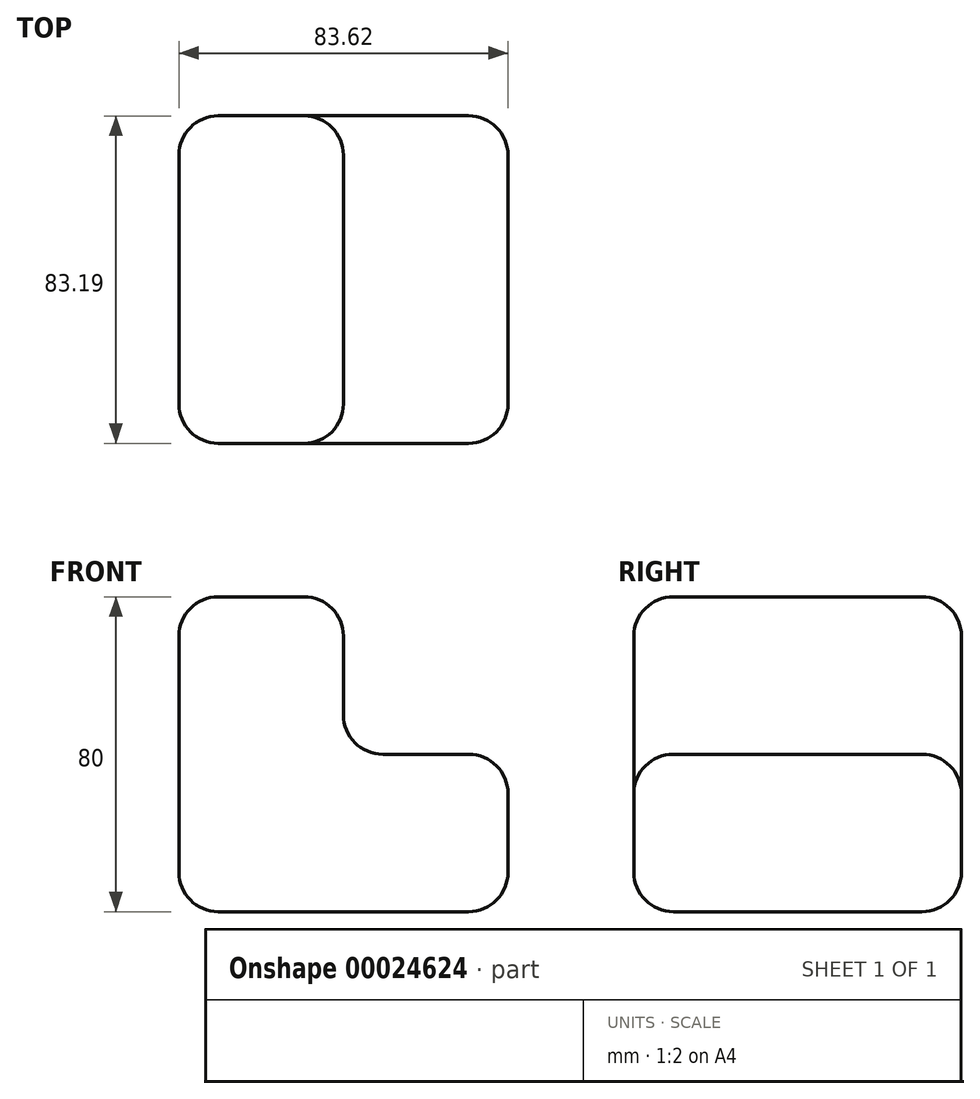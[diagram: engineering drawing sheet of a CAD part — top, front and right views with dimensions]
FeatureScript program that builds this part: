
annotation { "Feature Type Name" : "Feature", "Feature Type Description" : "" }
export const myFeature = defineFeature(function(context is Context, id is Id, definition is map)
    precondition{}
    {
        {
            var Q0;
            Q0=qCreatedBy(makeId("Top.planeOp"),FACE);
            var sketch = newSketch(context, id + "F0", { "sketchPlane" : qUnion([Q0])});
            skLineSegment(sketch, "E0.bottom", {"start": v(-59.13, -45.93) * mm, "end": v(24.5, -45.93) * mm});
            skLineSegment(sketch, "E0.top", {"start": v(-59.13, 37.26) * mm, "end": v(24.5, 37.26) * mm});
            skLineSegment(sketch, "E0.left", {"start": v(-59.13, -45.93) * mm, "end": v(-59.13, 37.26) * mm});
            skLineSegment(sketch, "E0.right", {"start": v(24.5, -45.93) * mm, "end": v(24.5, 37.26) * mm});
            skSolve(sketch);
        }
        {
            var Q0;
            Q0=makeQuery(id+"F0.imprint","IMPRINT",FACE,{"disambiguationData":[TD([[makeQuery(id+"F0.imprint","IMPRINT",EDGE,{"derivedFrom":sQuery(id+"F0.wireOp",EDGE,"E0.bottom")}),1.0]])]});
            extrude(context, id + "F1", {"entities" : qUnion([Q0]), "depth" : 40 * mm});
        }
        {
            var Q0;
            Q0=makeQuery(id+"F1.opExtrude","CAP_FACE",FACE,{"disambiguationData":[OSD([sQuery(id+"F0.wireOp",EDGE,"E0.bottom"),sQuery(id+"F0.wireOp",EDGE,"E0.top"),sQuery(id+"F0.wireOp",EDGE,"E0.left"),sQuery(id+"F0.wireOp",EDGE,"E0.right")])],"isStart":false});
            var sketch = newSketch(context, id + "F2", { "sketchPlane" : qUnion([Q0])});
            skLineSegment(sketch, "E1", {"start": v(-17.32, 37.26) * mm, "end": v(-17.32, -45.93) * mm});
            skSolve(sketch);
        }
        {
            var Q0;
            {var subQ1=sQuery(id+"F2.wireOp",EDGE,"E1");Q0=makeQuery(id+"F2.imprint","IMPRINT",FACE,{"disambiguationData":[TD([[makeQuery(id+"F2.imprint","IMPRINT",EDGE,{"derivedFrom":subQ1}),-1.0]])]});}
            extrude(context, id + "F3", {"entities" : qUnion([Q0]), "operationType" : NewBodyOperationType.ADD, "depth" : 40 * mm});
        }
        {
            var Q0;
            Q0=makeQuery(id+"F3.opExtrude","SWEPT_FACE",FACE,{"disambiguationData":[OSD([sQuery(id+"F2.wireOp",EDGE,"E1")])]});
            var Q1;
            Q1=makeQuery(id+"F3.opExtrude","SWEPT_EDGE",EDGE,{"disambiguationData":[OSD([sQuery(id+"F0.wireOp",EDGE,"E0.top"),sQuery(id+"F2.wireOp",EDGE,"E1")])]});
            var Q2;
            Q2=makeQuery(id+"F3.opExtrude","CAP_FACE",FACE,{"disambiguationData":[OSD([sQuery(id+"F0.wireOp",EDGE,"E0.bottom"),sQuery(id+"F0.wireOp",EDGE,"E0.top"),sQuery(id+"F0.wireOp",EDGE,"E0.left"),sQuery(id+"F2.wireOp",EDGE,"E1")])],"isStart":false});
            var Q3;
            Q3=makeQuery(id+"F3.opExtrude","SWEPT_EDGE",EDGE,{"disambiguationData":[OSD([sQuery(id+"F0.wireOp",EDGE,"E0.bottom"),sQuery(id+"F2.wireOp",EDGE,"E1")])]});
            var Q4;
            Q4=makeQuery(id+"F3.opExtrude","CAP_EDGE",EDGE,{"disambiguationData":[OSD([sQuery(id+"F2.wireOp",EDGE,"E1")])],"isStart":false});
            var Q5;
            {var subQ0=sQuery(id+"F0.wireOp",EDGE,"E0.bottom");Q5=makeQuery(id+"F3.boolean.opBoolean","MERGE",FACE,{"derivedFrom":[makeQuery(id+"F1.opExtrude","SWEPT_FACE",FACE,{"disambiguationData":[OSD([subQ0])]}),makeQuery(id+"F3.opExtrude","SWEPT_FACE",FACE,{"disambiguationData":[OSD([subQ0])]})]});}
            var Q6;
            {var subQ0=sQuery(id+"F0.wireOp",EDGE,"E0.bottom");var subQ1=sQuery(id+"F0.wireOp",EDGE,"E0.left");Q6=makeQuery(id+"F3.boolean.opBoolean","MERGE",EDGE,{"derivedFrom":[makeQuery(id+"F1.opExtrude","SWEPT_EDGE",EDGE,{"disambiguationData":[OSD([subQ0,subQ1])]}),makeQuery(id+"F3.opExtrude","SWEPT_EDGE",EDGE,{"disambiguationData":[OSD([subQ0,subQ1])]})]});}
            var Q7;
            Q7=makeQuery(id+"F3.opExtrude","CAP_EDGE",EDGE,{"disambiguationData":[OSD([sQuery(id+"F0.wireOp",EDGE,"E0.left")])],"isStart":false});
            var Q8;
            {var subQ0=sQuery(id+"F0.wireOp",EDGE,"E0.top");Q8=makeQuery(id+"F3.boolean.opBoolean","MERGE",FACE,{"derivedFrom":[makeQuery(id+"F1.opExtrude","SWEPT_FACE",FACE,{"disambiguationData":[OSD([subQ0])]}),makeQuery(id+"F3.opExtrude","SWEPT_FACE",FACE,{"disambiguationData":[OSD([subQ0])]})]});}
            var Q9;
            {var subQ0=sQuery(id+"F0.wireOp",EDGE,"E0.left");Q9=makeQuery(id+"F3.boolean.opBoolean","MERGE",FACE,{"derivedFrom":[makeQuery(id+"F1.opExtrude","SWEPT_FACE",FACE,{"disambiguationData":[OSD([subQ0])]}),makeQuery(id+"F3.opExtrude","SWEPT_FACE",FACE,{"disambiguationData":[OSD([subQ0])]})]});}
            var Q10;
            Q10=makeQuery(id+"F1.opExtrude","CAP_EDGE",EDGE,{"disambiguationData":[OSD([sQuery(id+"F0.wireOp",EDGE,"E0.bottom")])],"isStart":false});
            var Q11;
            Q11=makeQuery(id+"F3.opExtrude","CAP_EDGE",EDGE,{"disambiguationData":[OSD([sQuery(id+"F0.wireOp",EDGE,"E0.bottom")])],"isStart":false});
            var Q12;
            Q12=makeQuery(id+"F1.opExtrude","CAP_FACE",FACE,{"disambiguationData":[OSD([sQuery(id+"F0.wireOp",EDGE,"E0.bottom"),sQuery(id+"F0.wireOp",EDGE,"E0.top"),sQuery(id+"F0.wireOp",EDGE,"E0.left"),sQuery(id+"F0.wireOp",EDGE,"E0.right")])],"isStart":false});
            var Q13;
            Q13=makeQuery(id+"F1.opExtrude","CAP_EDGE",EDGE,{"disambiguationData":[OSD([sQuery(id+"F0.wireOp",EDGE,"E0.top")])],"isStart":false});
            var Q14;
            Q14=makeQuery(id+"F1.opExtrude","SWEPT_EDGE",EDGE,{"disambiguationData":[OSD([sQuery(id+"F0.wireOp",EDGE,"E0.top"),sQuery(id+"F0.wireOp",EDGE,"E0.right")])]});
            var Q15;
            Q15=makeQuery(id+"F3.opExtrude","CAP_EDGE",EDGE,{"disambiguationData":[OSD([sQuery(id+"F2.wireOp",EDGE,"E1")])],"isStart":true});
            var Q16;
            Q16=makeQuery(id+"F1.opExtrude","CAP_EDGE",EDGE,{"disambiguationData":[OSD([sQuery(id+"F0.wireOp",EDGE,"E0.bottom")])],"isStart":true});
            var Q17;
            Q17=makeQuery(id+"F1.opExtrude","SWEPT_FACE",FACE,{"disambiguationData":[OSD([sQuery(id+"F0.wireOp",EDGE,"E0.right")])]});
            var Q18;
            Q18=makeQuery(id+"F1.opExtrude","CAP_EDGE",EDGE,{"disambiguationData":[OSD([sQuery(id+"F0.wireOp",EDGE,"E0.right")])],"isStart":true});
            var Q19;
            Q19=makeQuery(id+"F1.opExtrude","CAP_EDGE",EDGE,{"disambiguationData":[OSD([sQuery(id+"F0.wireOp",EDGE,"E0.right")])],"isStart":false});
            var Q20;
            {var subQ0=sQuery(id+"F0.wireOp",EDGE,"E0.top");var subQ1=sQuery(id+"F0.wireOp",EDGE,"E0.left");Q20=makeQuery(id+"F3.boolean.opBoolean","MERGE",EDGE,{"derivedFrom":[makeQuery(id+"F1.opExtrude","SWEPT_EDGE",EDGE,{"disambiguationData":[OSD([subQ0,subQ1])]}),makeQuery(id+"F3.opExtrude","SWEPT_EDGE",EDGE,{"disambiguationData":[OSD([subQ0,subQ1])]})]});}
            var Q21;
            Q21=makeQuery(id+"F1.opExtrude","CAP_FACE",FACE,{"disambiguationData":[OSD([sQuery(id+"F0.wireOp",EDGE,"E0.bottom"),sQuery(id+"F0.wireOp",EDGE,"E0.top"),sQuery(id+"F0.wireOp",EDGE,"E0.left"),sQuery(id+"F0.wireOp",EDGE,"E0.right")])],"isStart":true});
            var Q22;
            Q22=makeQuery(id+"F1.opExtrude","SWEPT_EDGE",EDGE,{"disambiguationData":[OSD([sQuery(id+"F0.wireOp",EDGE,"E0.bottom"),sQuery(id+"F0.wireOp",EDGE,"E0.right")])]});
            var Q23;
            Q23=makeQuery(id+"F3.opExtrude","CAP_EDGE",EDGE,{"disambiguationData":[OSD([sQuery(id+"F0.wireOp",EDGE,"E0.top")])],"isStart":false});
            var Q24;
            Q24=makeQuery(id+"F1.opExtrude","CAP_EDGE",EDGE,{"disambiguationData":[OSD([sQuery(id+"F0.wireOp",EDGE,"E0.top")])],"isStart":true});
            var Q25;
            Q25=makeQuery(id+"F1.opExtrude","CAP_EDGE",EDGE,{"disambiguationData":[OSD([sQuery(id+"F0.wireOp",EDGE,"E0.left")])],"isStart":true});
            fillet(context, id + "F4", {"entities" : qUnion([Q0, Q1, Q2, Q3, Q4, Q5, Q6, Q7, Q8, Q9, Q10, Q11, Q12, Q13, Q14, Q15, Q16, Q17, Q18, Q19, Q20, Q21, Q22, Q23, Q24, Q25]), "radius" : 10 * mm, "tangentPropagation" : true, "allowEdgeOverflow" : false});
        }
    });
